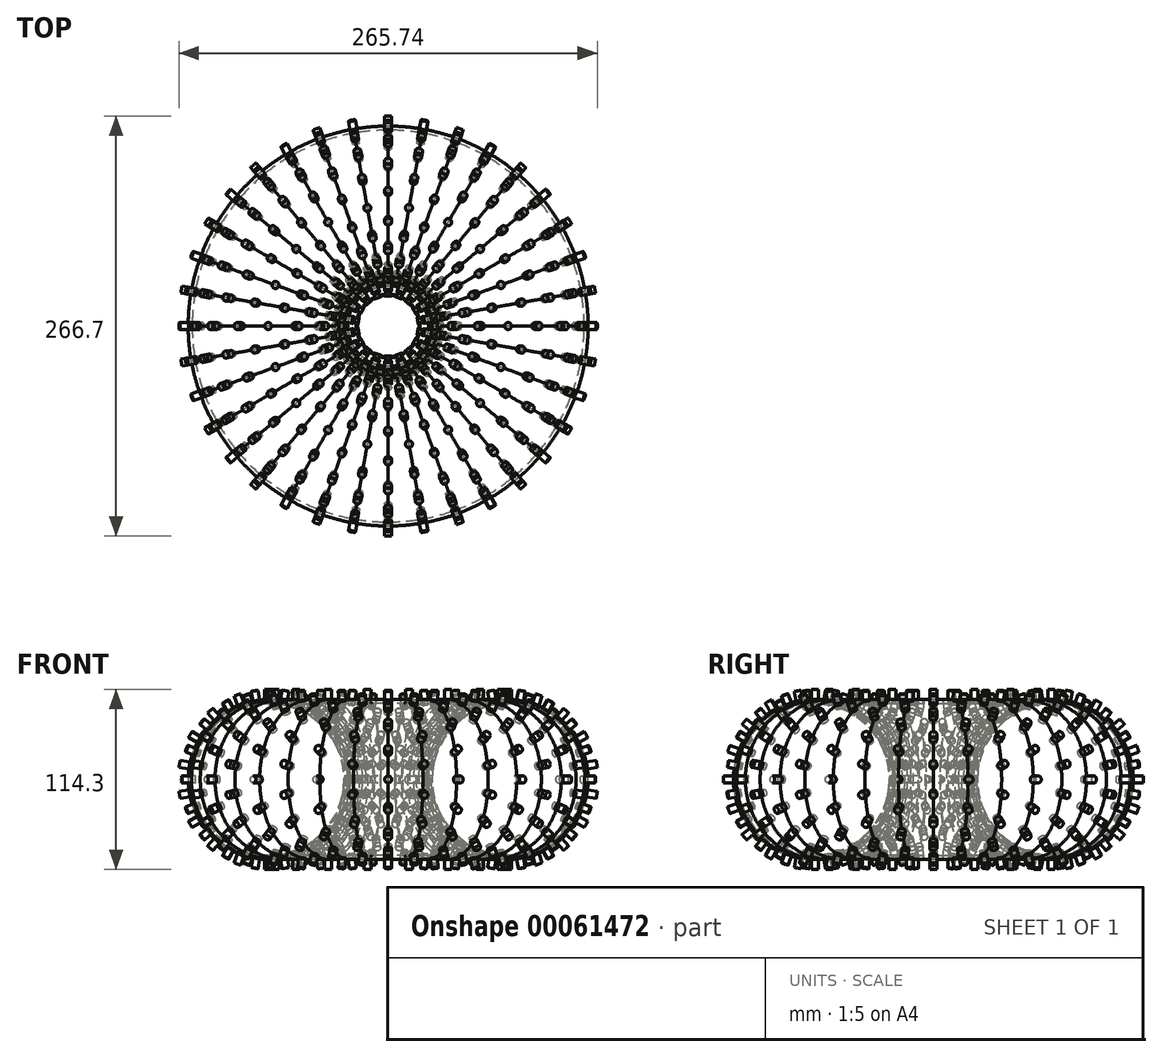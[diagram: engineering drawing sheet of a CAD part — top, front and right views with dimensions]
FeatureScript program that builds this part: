
annotation { "Feature Type Name" : "Feature", "Feature Type Description" : "" }
export const myFeature = defineFeature(function(context is Context, id is Id, definition is map)
    precondition{}
    {
        {
            var Q0;
            Q0=qCreatedBy(makeId("Top.planeOp"),FACE);
            var sketch = newSketch(context, id + "F0", { "sketchPlane" : qUnion([Q0])});
            skCircle(sketch, "E0", {"center": v(0, 0) * mm, "radius": 76.2 * mm});
            skCircle(sketch, "E1", {"center": v(0, 0) * mm, "radius": 25.4 * mm});
            skCircle(sketch, "E2", {"center": v(0, 0) * mm, "radius": 127 * mm});
            skSolve(sketch);
        }
        {
            var Q0;
            Q0=qCreatedBy(makeId("Front.planeOp"),FACE);
            cPlane(context, id + "F1", {"entities" : qUnion([Q0]), "cplaneType" : CPlaneType.OFFSET, "offset" : 25.4 * mm, "width" : 152.4 * mm, "height" : 152.4 * mm});
        }
        {
            var Q0;
            Q0=qCreatedBy(id+"F1.planeOp",FACE);
            cPlane(context, id + "F2", {"entities" : qUnion([Q0]), "cplaneType" : CPlaneType.OFFSET, "offset" : 101.6 * mm, "width" : 152.4 * mm, "height" : 152.4 * mm});
        }
        {
            var Q0;
            Q0=qCreatedBy(makeId("Right.planeOp"),FACE);
            var sketch = newSketch(context, id + "F3", { "sketchPlane" : qUnion([Q0])});
            skCircle(sketch, "E3", {"center": v(-76.2, 0) * mm, "radius": 50.8 * mm});
            skCircle(sketch, "E4", {"center": v(-76.2, 0) * mm, "radius": 48.26 * mm});
            skSolve(sketch);
        }
        {
            var Q0;
            Q0=makeQuery(id+"F3.imprint","IMPRINT",FACE,{"disambiguationData":[TD([[makeQuery(id+"F3.imprint","IMPRINT",EDGE,{"derivedFrom":sQuery(id+"F3.wireOp",EDGE,"E3")}),1.0]])]});
            var Q1;
            Q1=sQuery(id+"F0.wireOp",EDGE,"E0");
            revolve(context, id + "F4", {"entities" : qUnion([Q0]), "axis" : qUnion([Q1]), "revolveType" : RevolveType.ONE_DIRECTION, "oppositeDirection" : true, "angle" : 10 * degree});
        }
        {
            var Q0;
            Q0=makeQuery(id+"F4.opRevolve","SWEPT_BODY",BODY,{"disambiguationData":[OSD([sQuery(id+"F3.wireOp",EDGE,"E3"),sQuery(id+"F3.wireOp",EDGE,"E4")])]});
            var Q1;
            Q1=sQuery(id+"F0.wireOp",EDGE,"E0");
            circularPattern(context, id + "F5", {"entities" : qUnion([Q0]), "axis" : qUnion([Q1]), "angle" : 10 * degree, "instanceCount" : 36, "oppositeDirection" : true});
        }
        {
            var Q0;
            Q0=sQuery(id+"F0.wireOp",EDGE,"E0");
            var Q1;
            Q1=makeQuery(id+"F4.opRevolve","CAP_EDGE",EDGE,{"disambiguationData":[OSD([sQuery(id+"F3.wireOp",EDGE,"E3")])],"isStart":false});
            cPlane(context, id + "F6", {"entities" : qUnion([Q0, Q1]), "cplaneType" : CPlaneType.LINE_ANGLE, "offset" : 152.4 * mm, "angle" : 0 * degree, "width" : 152.4 * mm, "height" : 152.4 * mm});
        }
        {
            var Q0;
            Q0=qCreatedBy(id+"F6.planeOp",FACE);
            cPlane(context, id + "F7", {"entities" : qUnion([Q0]), "cplaneType" : CPlaneType.OFFSET, "offset" : 76.2 * mm, "oppositeDirection" : true, "width" : 152.4 * mm, "height" : 152.4 * mm});
        }
        {
            var Q0;
            Q0=qCreatedBy(id+"F7.planeOp",FACE);
            var sketch = newSketch(context, id + "F8", { "sketchPlane" : qUnion([Q0])});
            skLineSegment(sketch, "E5", {"start": v(29.1, 0) * mm, "end": v(-33.87, 0) * mm});
            skSolve(sketch);
        }
        {
            var Q0;
            Q0=qCreatedBy(id+"F7.planeOp",FACE);
            var Q1;
            Q1=sQuery(id+"F8.wireOp",EDGE,"E5");
            cPlane(context, id + "F9", {"entities" : qUnion([Q0, Q1]), "cplaneType" : CPlaneType.LINE_ANGLE, "offset" : 152.4 * mm, "angle" : 10 * degree, "width" : 152.4 * mm, "height" : 152.4 * mm});
        }
        {
            var Q0;
            Q0=qCreatedBy(id+"F9.planeOp",FACE);
            cPlane(context, id + "F10", {"entities" : qUnion([Q0]), "cplaneType" : CPlaneType.OFFSET, "offset" : 50.8 * mm, "width" : 152.4 * mm, "height" : 152.4 * mm});
        }
        {
            var Q0;
            Q0=qCreatedBy(id+"F2.planeOp",FACE);
            var sketch = newSketch(context, id + "F11", { "sketchPlane" : qUnion([Q0])});
            skCircle(sketch, "E6", {"center": v(0, 0) * mm, "radius": 2.22 * mm});
            skSolve(sketch);
        }
        {
            var Q0;
            Q0=makeQuery(id+"F11.imprint","IMPRINT",FACE,{"disambiguationData":[TD([[makeQuery(id+"F11.imprint","IMPRINT",EDGE,{"derivedFrom":sQuery(id+"F11.wireOp",EDGE,"E6")}),1.0]])]});
            extrude(context, id + "F12", {"entities" : qUnion([Q0]), "depth" : 6.35 * mm});
        }
        {
            var Q0;
            Q0 = qSketchRegion(id + "F11", true);
            var Q1;
            Q1=makeQuery(id+"F4.opRevolve","SWEPT_BODY",BODY,{"disambiguationData":[OSD([sQuery(id+"F3.wireOp",EDGE,"5e988a43-9d18-4499-b04f-da67374f12c3.0"),sQuery(id+"F3.wireOp",EDGE,"5e988a43-9d18-4499-b04f-da67374f12c3.1"),sQuery(id+"F3.wireOp",EDGE,"5e988a43-9d18-4499-b04f-da67374f12c3.2"),sQuery(id+"F3.wireOp",EDGE,"5e988a43-9d18-4499-b04f-da67374f12c3.3"),sQuery(id+"F3.wireOp",EDGE,"5e988a43-9d18-4499-b04f-da67374f12c3.4"),sQuery(id+"F3.wireOp",EDGE,"5e988a43-9d18-4499-b04f-da67374f12c3.5"),sQuery(id+"F3.wireOp",EDGE,"5e988a43-9d18-4499-b04f-da67374f12c3.6"),sQuery(id+"F3.wireOp",EDGE,"5e988a43-9d18-4499-b04f-da67374f12c3.7"),sQuery(id+"F3.wireOp",EDGE,"5e988a43-9d18-4499-b04f-da67374f12c3.8"),sQuery(id+"F3.wireOp",EDGE,"5e988a43-9d18-4499-b04f-da67374f12c3.9"),sQuery(id+"F3.wireOp",EDGE,"5e988a43-9d18-4499-b04f-da67374f12c3.10"),sQuery(id+"F3.wireOp",EDGE,"5e988a43-9d18-4499-b04f-da67374f12c3.11"),sQuery(id+"F3.wireOp",EDGE,"5e988a43-9d18-4499-b04f-da67374f12c3.12"),sQuery(id+"F3.wireOp",EDGE,"5e988a43-9d18-4499-b04f-da67374f12c3.13"),sQuery(id+"F3.wireOp",EDGE,"5e988a43-9d18-4499-b04f-da67374f12c3.14"),sQuery(id+"F3.wireOp",EDGE,"5e988a43-9d18-4499-b04f-da67374f12c3.15"),sQuery(id+"F3.wireOp",EDGE,"5e988a43-9d18-4499-b04f-da67374f12c3.16"),sQuery(id+"F3.wireOp",EDGE,"5e988a43-9d18-4499-b04f-da67374f12c3.17"),sQuery(id+"F3.wireOp",EDGE,"5e988a43-9d18-4499-b04f-da67374f12c3.18"),sQuery(id+"F3.wireOp",EDGE,"5e988a43-9d18-4499-b04f-da67374f12c3.19"),sQuery(id+"F3.wireOp",EDGE,"5e988a43-9d18-4499-b04f-da67374f12c3.20"),sQuery(id+"F3.wireOp",EDGE,"5e988a43-9d18-4499-b04f-da67374f12c3.21"),sQuery(id+"F3.wireOp",EDGE,"5e988a43-9d18-4499-b04f-da67374f12c3.22"),sQuery(id+"F3.wireOp",EDGE,"5e988a43-9d18-4499-b04f-da67374f12c3.23"),sQuery(id+"F3.wireOp",EDGE,"5e988a43-9d18-4499-b04f-da67374f12c3.24"),sQuery(id+"F3.wireOp",EDGE,"5e988a43-9d18-4499-b04f-da67374f12c3.25"),sQuery(id+"F3.wireOp",EDGE,"5e988a43-9d18-4499-b04f-da67374f12c3.26"),sQuery(id+"F3.wireOp",EDGE,"5e988a43-9d18-4499-b04f-da67374f12c3.27"),sQuery(id+"F3.wireOp",EDGE,"5e988a43-9d18-4499-b04f-da67374f12c3.28"),sQuery(id+"F3.wireOp",EDGE,"5e988a43-9d18-4499-b04f-da67374f12c3.29"),sQuery(id+"F3.wireOp",EDGE,"5e988a43-9d18-4499-b04f-da67374f12c3.30"),sQuery(id+"F3.wireOp",EDGE,"5e988a43-9d18-4499-b04f-da67374f12c3.31"),sQuery(id+"F3.wireOp",EDGE,"5e988a43-9d18-4499-b04f-da67374f12c3.32"),sQuery(id+"F3.wireOp",EDGE,"5e988a43-9d18-4499-b04f-da67374f12c3.33"),sQuery(id+"F3.wireOp",EDGE,"5e988a43-9d18-4499-b04f-da67374f12c3.34"),sQuery(id+"F3.wireOp",EDGE,"5e988a43-9d18-4499-b04f-da67374f12c3.35"),sQuery(id+"F3.wireOp",EDGE,"b20bae4d-07ca-4f3f-87bb-0b12c9c8b110.0"),sQuery(id+"F3.wireOp",EDGE,"b20bae4d-07ca-4f3f-87bb-0b12c9c8b110.1"),sQuery(id+"F3.wireOp",EDGE,"b20bae4d-07ca-4f3f-87bb-0b12c9c8b110.2"),sQuery(id+"F3.wireOp",EDGE,"b20bae4d-07ca-4f3f-87bb-0b12c9c8b110.3"),sQuery(id+"F3.wireOp",EDGE,"b20bae4d-07ca-4f3f-87bb-0b12c9c8b110.4"),sQuery(id+"F3.wireOp",EDGE,"b20bae4d-07ca-4f3f-87bb-0b12c9c8b110.5"),sQuery(id+"F3.wireOp",EDGE,"b20bae4d-07ca-4f3f-87bb-0b12c9c8b110.6"),sQuery(id+"F3.wireOp",EDGE,"b20bae4d-07ca-4f3f-87bb-0b12c9c8b110.7"),sQuery(id+"F3.wireOp",EDGE,"b20bae4d-07ca-4f3f-87bb-0b12c9c8b110.8"),sQuery(id+"F3.wireOp",EDGE,"b20bae4d-07ca-4f3f-87bb-0b12c9c8b110.9"),sQuery(id+"F3.wireOp",EDGE,"b20bae4d-07ca-4f3f-87bb-0b12c9c8b110.10"),sQuery(id+"F3.wireOp",EDGE,"b20bae4d-07ca-4f3f-87bb-0b12c9c8b110.11"),sQuery(id+"F3.wireOp",EDGE,"b20bae4d-07ca-4f3f-87bb-0b12c9c8b110.12"),sQuery(id+"F3.wireOp",EDGE,"b20bae4d-07ca-4f3f-87bb-0b12c9c8b110.13"),sQuery(id+"F3.wireOp",EDGE,"b20bae4d-07ca-4f3f-87bb-0b12c9c8b110.14"),sQuery(id+"F3.wireOp",EDGE,"b20bae4d-07ca-4f3f-87bb-0b12c9c8b110.15"),sQuery(id+"F3.wireOp",EDGE,"b20bae4d-07ca-4f3f-87bb-0b12c9c8b110.16"),sQuery(id+"F3.wireOp",EDGE,"b20bae4d-07ca-4f3f-87bb-0b12c9c8b110.17"),sQuery(id+"F3.wireOp",EDGE,"b20bae4d-07ca-4f3f-87bb-0b12c9c8b110.18"),sQuery(id+"F3.wireOp",EDGE,"b20bae4d-07ca-4f3f-87bb-0b12c9c8b110.19"),sQuery(id+"F3.wireOp",EDGE,"b20bae4d-07ca-4f3f-87bb-0b12c9c8b110.20"),sQuery(id+"F3.wireOp",EDGE,"b20bae4d-07ca-4f3f-87bb-0b12c9c8b110.21"),sQuery(id+"F3.wireOp",EDGE,"b20bae4d-07ca-4f3f-87bb-0b12c9c8b110.22"),sQuery(id+"F3.wireOp",EDGE,"b20bae4d-07ca-4f3f-87bb-0b12c9c8b110.23"),sQuery(id+"F3.wireOp",EDGE,"b20bae4d-07ca-4f3f-87bb-0b12c9c8b110.24"),sQuery(id+"F3.wireOp",EDGE,"b20bae4d-07ca-4f3f-87bb-0b12c9c8b110.25"),sQuery(id+"F3.wireOp",EDGE,"b20bae4d-07ca-4f3f-87bb-0b12c9c8b110.26"),sQuery(id+"F3.wireOp",EDGE,"b20bae4d-07ca-4f3f-87bb-0b12c9c8b110.27"),sQuery(id+"F3.wireOp",EDGE,"b20bae4d-07ca-4f3f-87bb-0b12c9c8b110.28"),sQuery(id+"F3.wireOp",EDGE,"b20bae4d-07ca-4f3f-87bb-0b12c9c8b110.29"),sQuery(id+"F3.wireOp",EDGE,"b20bae4d-07ca-4f3f-87bb-0b12c9c8b110.30"),sQuery(id+"F3.wireOp",EDGE,"b20bae4d-07ca-4f3f-87bb-0b12c9c8b110.31"),sQuery(id+"F3.wireOp",EDGE,"b20bae4d-07ca-4f3f-87bb-0b12c9c8b110.32"),sQuery(id+"F3.wireOp",EDGE,"b20bae4d-07ca-4f3f-87bb-0b12c9c8b110.33"),sQuery(id+"F3.wireOp",EDGE,"b20bae4d-07ca-4f3f-87bb-0b12c9c8b110.34"),sQuery(id+"F3.wireOp",EDGE,"b20bae4d-07ca-4f3f-87bb-0b12c9c8b110.35")])]});
            extrude(context, id + "F13", {"entities" : qUnion([Q0]), "oppositeDirection" : true, "endBoundEntityBody" : qUnion([Q1]), "depth" : 2.54 * mm});
        }
        {
            var Q0;
            Q0=qCreatedBy(id+"F10.planeOp",FACE);
            var sketch = newSketch(context, id + "F14", { "sketchPlane" : qUnion([Q0])});
            skCircle(sketch, "E7", {"center": v(-0.4, 13.23) * mm, "radius": 2.22 * mm});
            skSolve(sketch);
        }
        {
            var Q0;
            Q0=makeQuery(id+"F14.imprint","IMPRINT",FACE,{"disambiguationData":[TD([[makeQuery(id+"F14.imprint","IMPRINT",EDGE,{"derivedFrom":sQuery(id+"F14.wireOp",EDGE,"E7")}),1.0]])]});
            extrude(context, id + "F15", {"entities" : qUnion([Q0]), "depth" : 6.35 * mm});
        }
        {
            var Q0;
            Q0 = qSketchRegion(id + "F14", true);
            extrude(context, id + "F16", {"entities" : qUnion([Q0]), "oppositeDirection" : true, "depth" : 2.54 * mm});
        }
        {
            var Q0;
            Q0=makeQuery(id+"F12.opExtrude","SWEPT_BODY",BODY,{"disambiguationData":[OSD([sQuery(id+"F11.wireOp",EDGE,"E6")])]});
            var Q1;
            Q1=makeQuery(id+"F13.opExtrude","SWEPT_BODY",BODY,{"disambiguationData":[OSD([sQuery(id+"F11.wireOp",EDGE,"E6")])]});
            var Q2;
            Q2=sQuery(id+"F0.wireOp",EDGE,"E0");
            circularPattern(context, id + "F17", {"entities" : qUnion([Q0, Q1]), "axis" : qUnion([Q2]), "angle" : 20 * degree, "instanceCount" : 18, "oppositeDirection" : true});
        }
        {
            var Q0;
            Q0=makeQuery(id+"F15.opExtrude","SWEPT_BODY",BODY,{"disambiguationData":[OSD([sQuery(id+"F14.wireOp",EDGE,"E7")])]});
            var Q1;
            Q1=makeQuery(id+"F16.opExtrude","SWEPT_BODY",BODY,{"disambiguationData":[OSD([sQuery(id+"F14.wireOp",EDGE,"E7")])]});
            var Q2;
            Q2=sQuery(id+"F0.wireOp",EDGE,"E0");
            circularPattern(context, id + "F18", {"entities" : qUnion([Q0, Q1]), "axis" : qUnion([Q2]), "angle" : 20 * degree, "instanceCount" : 18});
        }
        {
            var Q0;
            Q0=makeQuery(id+"F18.opPattern","COPY",BODY,{"derivedFrom":makeQuery(id+"F15.opExtrude","SWEPT_BODY",BODY,{"disambiguationData":[OSD([sQuery(id+"F14.wireOp",EDGE,"E7")])]}),"instanceName":"16"});
            var Q1;
            Q1=makeQuery(id+"F18.opPattern","COPY",BODY,{"derivedFrom":makeQuery(id+"F16.opExtrude","SWEPT_BODY",BODY,{"disambiguationData":[OSD([sQuery(id+"F14.wireOp",EDGE,"E7")])]}),"instanceName":"16"});
            var Q2;
            Q2=makeQuery(id+"F5.opPattern","COPY",EDGE,{"derivedFrom":makeQuery(id+"F4.opRevolve","CAP_EDGE",EDGE,{"disambiguationData":[OSD([sQuery(id+"F3.wireOp",EDGE,"E3")])],"isStart":true}),"instanceName":"5"});
            circularPattern(context, id + "F19", {"entities" : qUnion([Q0, Q1]), "axis" : qUnion([Q2]), "angle" : 20 * degree, "instanceCount" : 18});
        }
        {
            var Q0;
            Q0=makeQuery(id+"F17.opPattern","COPY",BODY,{"derivedFrom":makeQuery(id+"F12.opExtrude","SWEPT_BODY",BODY,{"disambiguationData":[OSD([sQuery(id+"F11.wireOp",EDGE,"E6")])]}),"instanceName":"3"});
            var Q1;
            Q1=makeQuery(id+"F17.opPattern","COPY",BODY,{"derivedFrom":makeQuery(id+"F13.opExtrude","SWEPT_BODY",BODY,{"disambiguationData":[OSD([sQuery(id+"F11.wireOp",EDGE,"E6")])]}),"instanceName":"3"});
            var Q2;
            Q2=makeQuery(id+"F5.opPattern","COPY",EDGE,{"derivedFrom":makeQuery(id+"F4.opRevolve","CAP_EDGE",EDGE,{"disambiguationData":[OSD([sQuery(id+"F3.wireOp",EDGE,"E3")])],"isStart":false}),"instanceName":"5"});
            circularPattern(context, id + "F20", {"entities" : qUnion([Q0, Q1]), "axis" : qUnion([Q2]), "angle" : 20 * degree, "instanceCount" : 18});
        }
        {
            var Q0;
            Q0=makeQuery(id+"F18.opPattern","COPY",BODY,{"derivedFrom":makeQuery(id+"F16.opExtrude","SWEPT_BODY",BODY,{"disambiguationData":[OSD([sQuery(id+"F14.wireOp",EDGE,"E7")])]}),"instanceName":"15"});
            var Q1;
            Q1=makeQuery(id+"F18.opPattern","COPY",BODY,{"derivedFrom":makeQuery(id+"F15.opExtrude","SWEPT_BODY",BODY,{"disambiguationData":[OSD([sQuery(id+"F14.wireOp",EDGE,"E7")])]}),"instanceName":"15"});
            var Q2;
            Q2=makeQuery(id+"F5.opPattern","COPY",EDGE,{"derivedFrom":makeQuery(id+"F4.opRevolve","CAP_EDGE",EDGE,{"disambiguationData":[OSD([sQuery(id+"F3.wireOp",EDGE,"E3")])],"isStart":false}),"instanceName":"6"});
            circularPattern(context, id + "F21", {"entities" : qUnion([Q0, Q1]), "axis" : qUnion([Q2]), "angle" : 20 * degree, "instanceCount" : 18});
        }
        {
            var Q0;
            Q0=makeQuery(id+"F17.opPattern","COPY",BODY,{"derivedFrom":makeQuery(id+"F12.opExtrude","SWEPT_BODY",BODY,{"disambiguationData":[OSD([sQuery(id+"F11.wireOp",EDGE,"E6")])]}),"instanceName":"4"});
            var Q1;
            Q1=makeQuery(id+"F17.opPattern","COPY",BODY,{"derivedFrom":makeQuery(id+"F13.opExtrude","SWEPT_BODY",BODY,{"disambiguationData":[OSD([sQuery(id+"F11.wireOp",EDGE,"E6")])]}),"instanceName":"4"});
            var Q2;
            Q2=makeQuery(id+"F5.opPattern","COPY",EDGE,{"derivedFrom":makeQuery(id+"F4.opRevolve","CAP_EDGE",EDGE,{"disambiguationData":[OSD([sQuery(id+"F3.wireOp",EDGE,"E3")])],"isStart":false}),"instanceName":"7"});
            circularPattern(context, id + "F22", {"entities" : qUnion([Q0, Q1]), "axis" : qUnion([Q2]), "angle" : 20 * degree, "instanceCount" : 18});
        }
        {
            var Q0;
            Q0=makeQuery(id+"F18.opPattern","COPY",BODY,{"derivedFrom":makeQuery(id+"F15.opExtrude","SWEPT_BODY",BODY,{"disambiguationData":[OSD([sQuery(id+"F14.wireOp",EDGE,"E7")])]}),"instanceName":"14"});
            var Q1;
            Q1=makeQuery(id+"F18.opPattern","COPY",BODY,{"derivedFrom":makeQuery(id+"F16.opExtrude","SWEPT_BODY",BODY,{"disambiguationData":[OSD([sQuery(id+"F14.wireOp",EDGE,"E7")])]}),"instanceName":"14"});
            var Q2;
            Q2=makeQuery(id+"F5.opPattern","COPY",EDGE,{"derivedFrom":makeQuery(id+"F4.opRevolve","CAP_EDGE",EDGE,{"disambiguationData":[OSD([sQuery(id+"F3.wireOp",EDGE,"E3")])],"isStart":true}),"instanceName":"9"});
            circularPattern(context, id + "F23", {"entities" : qUnion([Q0, Q1]), "axis" : qUnion([Q2]), "angle" : 20 * degree, "instanceCount" : 18});
        }
        {
            var Q0;
            Q0=makeQuery(id+"F17.opPattern","COPY",BODY,{"derivedFrom":makeQuery(id+"F12.opExtrude","SWEPT_BODY",BODY,{"disambiguationData":[OSD([sQuery(id+"F11.wireOp",EDGE,"E6")])]}),"instanceName":"5"});
            var Q1;
            Q1=makeQuery(id+"F17.opPattern","COPY",BODY,{"derivedFrom":makeQuery(id+"F13.opExtrude","SWEPT_BODY",BODY,{"disambiguationData":[OSD([sQuery(id+"F11.wireOp",EDGE,"E6")])]}),"instanceName":"5"});
            var Q2;
            Q2=makeQuery(id+"F5.opPattern","COPY",EDGE,{"derivedFrom":makeQuery(id+"F4.opRevolve","CAP_EDGE",EDGE,{"disambiguationData":[OSD([sQuery(id+"F3.wireOp",EDGE,"E3")])],"isStart":true}),"instanceName":"10"});
            circularPattern(context, id + "F24", {"entities" : qUnion([Q0, Q1]), "axis" : qUnion([Q2]), "angle" : 20 * degree, "instanceCount" : 18});
        }
        {
            var Q0;
            Q0=makeQuery(id+"F18.opPattern","COPY",BODY,{"derivedFrom":makeQuery(id+"F15.opExtrude","SWEPT_BODY",BODY,{"disambiguationData":[OSD([sQuery(id+"F14.wireOp",EDGE,"E7")])]}),"instanceName":"13"});
            var Q1;
            Q1=makeQuery(id+"F18.opPattern","COPY",BODY,{"derivedFrom":makeQuery(id+"F16.opExtrude","SWEPT_BODY",BODY,{"disambiguationData":[OSD([sQuery(id+"F14.wireOp",EDGE,"E7")])]}),"instanceName":"13"});
            var Q2;
            Q2=makeQuery(id+"F5.opPattern","COPY",EDGE,{"derivedFrom":makeQuery(id+"F4.opRevolve","CAP_EDGE",EDGE,{"disambiguationData":[OSD([sQuery(id+"F3.wireOp",EDGE,"E3")])],"isStart":true}),"instanceName":"11"});
            circularPattern(context, id + "F25", {"entities" : qUnion([Q0, Q1]), "axis" : qUnion([Q2]), "angle" : 20 * degree, "instanceCount" : 18});
        }
        {
            var Q0;
            Q0=makeQuery(id+"F17.opPattern","COPY",BODY,{"derivedFrom":makeQuery(id+"F12.opExtrude","SWEPT_BODY",BODY,{"disambiguationData":[OSD([sQuery(id+"F11.wireOp",EDGE,"E6")])]}),"instanceName":"6"});
            var Q1;
            Q1=makeQuery(id+"F17.opPattern","COPY",BODY,{"derivedFrom":makeQuery(id+"F13.opExtrude","SWEPT_BODY",BODY,{"disambiguationData":[OSD([sQuery(id+"F11.wireOp",EDGE,"E6")])]}),"instanceName":"6"});
            var Q2;
            Q2=makeQuery(id+"F5.opPattern","COPY",EDGE,{"derivedFrom":makeQuery(id+"F4.opRevolve","CAP_EDGE",EDGE,{"disambiguationData":[OSD([sQuery(id+"F3.wireOp",EDGE,"E3")])],"isStart":true}),"instanceName":"12"});
            circularPattern(context, id + "F26", {"entities" : qUnion([Q0, Q1]), "axis" : qUnion([Q2]), "angle" : 20 * degree, "instanceCount" : 18});
        }
        {
            var Q0;
            Q0=makeQuery(id+"F18.opPattern","COPY",BODY,{"derivedFrom":makeQuery(id+"F15.opExtrude","SWEPT_BODY",BODY,{"disambiguationData":[OSD([sQuery(id+"F14.wireOp",EDGE,"E7")])]}),"instanceName":"12"});
            var Q1;
            Q1=makeQuery(id+"F18.opPattern","COPY",BODY,{"derivedFrom":makeQuery(id+"F16.opExtrude","SWEPT_BODY",BODY,{"disambiguationData":[OSD([sQuery(id+"F14.wireOp",EDGE,"E7")])]}),"instanceName":"12"});
            var Q2;
            Q2=makeQuery(id+"F5.opPattern","COPY",EDGE,{"derivedFrom":makeQuery(id+"F4.opRevolve","CAP_EDGE",EDGE,{"disambiguationData":[OSD([sQuery(id+"F3.wireOp",EDGE,"E3")])],"isStart":true}),"instanceName":"13"});
            circularPattern(context, id + "F27", {"entities" : qUnion([Q0, Q1]), "axis" : qUnion([Q2]), "angle" : 20 * degree, "instanceCount" : 18});
        }
        {
            var Q0;
            Q0=makeQuery(id+"F17.opPattern","COPY",BODY,{"derivedFrom":makeQuery(id+"F13.opExtrude","SWEPT_BODY",BODY,{"disambiguationData":[OSD([sQuery(id+"F11.wireOp",EDGE,"E6")])]}),"instanceName":"7"});
            var Q1;
            Q1=makeQuery(id+"F17.opPattern","COPY",BODY,{"derivedFrom":makeQuery(id+"F12.opExtrude","SWEPT_BODY",BODY,{"disambiguationData":[OSD([sQuery(id+"F11.wireOp",EDGE,"E6")])]}),"instanceName":"7"});
            var Q2;
            Q2=makeQuery(id+"F5.opPattern","COPY",EDGE,{"derivedFrom":makeQuery(id+"F4.opRevolve","CAP_EDGE",EDGE,{"disambiguationData":[OSD([sQuery(id+"F3.wireOp",EDGE,"E3")])],"isStart":false}),"instanceName":"13"});
            circularPattern(context, id + "F28", {"entities" : qUnion([Q0, Q1]), "axis" : qUnion([Q2]), "angle" : 20 * degree, "instanceCount" : 18});
        }
        {
            var Q0;
            Q0=makeQuery(id+"F18.opPattern","COPY",BODY,{"derivedFrom":makeQuery(id+"F16.opExtrude","SWEPT_BODY",BODY,{"disambiguationData":[OSD([sQuery(id+"F14.wireOp",EDGE,"E7")])]}),"instanceName":"11"});
            var Q1;
            Q1=makeQuery(id+"F18.opPattern","COPY",BODY,{"derivedFrom":makeQuery(id+"F15.opExtrude","SWEPT_BODY",BODY,{"disambiguationData":[OSD([sQuery(id+"F14.wireOp",EDGE,"E7")])]}),"instanceName":"11"});
            var Q2;
            Q2=makeQuery(id+"F5.opPattern","COPY",EDGE,{"derivedFrom":makeQuery(id+"F4.opRevolve","CAP_EDGE",EDGE,{"disambiguationData":[OSD([sQuery(id+"F3.wireOp",EDGE,"E3")])],"isStart":false}),"instanceName":"14"});
            circularPattern(context, id + "F29", {"entities" : qUnion([Q0, Q1]), "axis" : qUnion([Q2]), "angle" : 20 * degree, "instanceCount" : 18});
        }
        {
            var Q0;
            Q0=makeQuery(id+"F17.opPattern","COPY",BODY,{"derivedFrom":makeQuery(id+"F13.opExtrude","SWEPT_BODY",BODY,{"disambiguationData":[OSD([sQuery(id+"F11.wireOp",EDGE,"E6")])]}),"instanceName":"8"});
            var Q1;
            Q1=makeQuery(id+"F17.opPattern","COPY",BODY,{"derivedFrom":makeQuery(id+"F12.opExtrude","SWEPT_BODY",BODY,{"disambiguationData":[OSD([sQuery(id+"F11.wireOp",EDGE,"E6")])]}),"instanceName":"8"});
            var Q2;
            Q2=makeQuery(id+"F5.opPattern","COPY",EDGE,{"derivedFrom":makeQuery(id+"F4.opRevolve","CAP_EDGE",EDGE,{"disambiguationData":[OSD([sQuery(id+"F3.wireOp",EDGE,"E3")])],"isStart":false}),"instanceName":"15"});
            circularPattern(context, id + "F30", {"entities" : qUnion([Q0, Q1]), "axis" : qUnion([Q2]), "angle" : 20 * degree, "instanceCount" : 18});
        }
        {
            var Q0;
            Q0=makeQuery(id+"F18.opPattern","COPY",BODY,{"derivedFrom":makeQuery(id+"F16.opExtrude","SWEPT_BODY",BODY,{"disambiguationData":[OSD([sQuery(id+"F14.wireOp",EDGE,"E7")])]}),"instanceName":"10"});
            var Q1;
            Q1=makeQuery(id+"F18.opPattern","COPY",BODY,{"derivedFrom":makeQuery(id+"F15.opExtrude","SWEPT_BODY",BODY,{"disambiguationData":[OSD([sQuery(id+"F14.wireOp",EDGE,"E7")])]}),"instanceName":"10"});
            var Q2;
            Q2=makeQuery(id+"F5.opPattern","COPY",EDGE,{"derivedFrom":makeQuery(id+"F4.opRevolve","CAP_EDGE",EDGE,{"disambiguationData":[OSD([sQuery(id+"F3.wireOp",EDGE,"E3")])],"isStart":false}),"instanceName":"16"});
            circularPattern(context, id + "F31", {"entities" : qUnion([Q0, Q1]), "axis" : qUnion([Q2]), "angle" : 20 * degree, "instanceCount" : 18});
        }
        {
            var Q0;
            Q0=makeQuery(id+"F17.opPattern","COPY",BODY,{"derivedFrom":makeQuery(id+"F13.opExtrude","SWEPT_BODY",BODY,{"disambiguationData":[OSD([sQuery(id+"F11.wireOp",EDGE,"E6")])]}),"instanceName":"9"});
            var Q1;
            Q1=makeQuery(id+"F17.opPattern","COPY",BODY,{"derivedFrom":makeQuery(id+"F12.opExtrude","SWEPT_BODY",BODY,{"disambiguationData":[OSD([sQuery(id+"F11.wireOp",EDGE,"E6")])]}),"instanceName":"9"});
            var Q2;
            Q2=makeQuery(id+"F5.opPattern","COPY",EDGE,{"derivedFrom":makeQuery(id+"F4.opRevolve","CAP_EDGE",EDGE,{"disambiguationData":[OSD([sQuery(id+"F3.wireOp",EDGE,"E3")])],"isStart":true}),"instanceName":"18"});
            circularPattern(context, id + "F32", {"entities" : qUnion([Q0, Q1]), "axis" : qUnion([Q2]), "angle" : 20 * degree, "instanceCount" : 18});
        }
        {
            var Q0;
            Q0=makeQuery(id+"F18.opPattern","COPY",BODY,{"derivedFrom":makeQuery(id+"F16.opExtrude","SWEPT_BODY",BODY,{"disambiguationData":[OSD([sQuery(id+"F14.wireOp",EDGE,"E7")])]}),"instanceName":"9"});
            var Q1;
            Q1=makeQuery(id+"F18.opPattern","COPY",BODY,{"derivedFrom":makeQuery(id+"F15.opExtrude","SWEPT_BODY",BODY,{"disambiguationData":[OSD([sQuery(id+"F14.wireOp",EDGE,"E7")])]}),"instanceName":"9"});
            var Q2;
            Q2=makeQuery(id+"F5.opPattern","COPY",EDGE,{"derivedFrom":makeQuery(id+"F4.opRevolve","CAP_EDGE",EDGE,{"disambiguationData":[OSD([sQuery(id+"F3.wireOp",EDGE,"E3")])],"isStart":true}),"instanceName":"19"});
            circularPattern(context, id + "F33", {"entities" : qUnion([Q0, Q1]), "axis" : qUnion([Q2]), "angle" : 20 * degree, "instanceCount" : 18});
        }
        {
            var Q0;
            Q0=makeQuery(id+"F17.opPattern","COPY",BODY,{"derivedFrom":makeQuery(id+"F12.opExtrude","SWEPT_BODY",BODY,{"disambiguationData":[OSD([sQuery(id+"F11.wireOp",EDGE,"E6")])]}),"instanceName":"10"});
            var Q1;
            Q1=makeQuery(id+"F17.opPattern","COPY",BODY,{"derivedFrom":makeQuery(id+"F13.opExtrude","SWEPT_BODY",BODY,{"disambiguationData":[OSD([sQuery(id+"F11.wireOp",EDGE,"E6")])]}),"instanceName":"10"});
            var Q2;
            Q2=makeQuery(id+"F5.opPattern","COPY",EDGE,{"derivedFrom":makeQuery(id+"F4.opRevolve","CAP_EDGE",EDGE,{"disambiguationData":[OSD([sQuery(id+"F3.wireOp",EDGE,"E3")])],"isStart":true}),"instanceName":"20"});
            circularPattern(context, id + "F34", {"entities" : qUnion([Q0, Q1]), "axis" : qUnion([Q2]), "angle" : 20 * degree, "instanceCount" : 18});
        }
        {
            var Q0;
            Q0=makeQuery(id+"F18.opPattern","COPY",BODY,{"derivedFrom":makeQuery(id+"F15.opExtrude","SWEPT_BODY",BODY,{"disambiguationData":[OSD([sQuery(id+"F14.wireOp",EDGE,"E7")])]}),"instanceName":"8"});
            var Q1;
            Q1=makeQuery(id+"F18.opPattern","COPY",BODY,{"derivedFrom":makeQuery(id+"F16.opExtrude","SWEPT_BODY",BODY,{"disambiguationData":[OSD([sQuery(id+"F14.wireOp",EDGE,"E7")])]}),"instanceName":"8"});
            var Q2;
            Q2=makeQuery(id+"F5.opPattern","COPY",EDGE,{"derivedFrom":makeQuery(id+"F4.opRevolve","CAP_EDGE",EDGE,{"disambiguationData":[OSD([sQuery(id+"F3.wireOp",EDGE,"E3")])],"isStart":true}),"instanceName":"21"});
            circularPattern(context, id + "F35", {"entities" : qUnion([Q0, Q1]), "axis" : qUnion([Q2]), "angle" : 20 * degree, "instanceCount" : 18});
        }
        {
            var Q0;
            Q0=makeQuery(id+"F17.opPattern","COPY",BODY,{"derivedFrom":makeQuery(id+"F13.opExtrude","SWEPT_BODY",BODY,{"disambiguationData":[OSD([sQuery(id+"F11.wireOp",EDGE,"E6")])]}),"instanceName":"11"});
            var Q1;
            Q1=makeQuery(id+"F17.opPattern","COPY",BODY,{"derivedFrom":makeQuery(id+"F12.opExtrude","SWEPT_BODY",BODY,{"disambiguationData":[OSD([sQuery(id+"F11.wireOp",EDGE,"E6")])]}),"instanceName":"11"});
            var Q2;
            Q2=makeQuery(id+"F5.opPattern","COPY",EDGE,{"derivedFrom":makeQuery(id+"F4.opRevolve","CAP_EDGE",EDGE,{"disambiguationData":[OSD([sQuery(id+"F3.wireOp",EDGE,"E3")])],"isStart":true}),"instanceName":"22"});
            circularPattern(context, id + "F36", {"entities" : qUnion([Q0, Q1]), "axis" : qUnion([Q2]), "angle" : 20 * degree, "instanceCount" : 18});
        }
        {
            var Q0;
            Q0=makeQuery(id+"F18.opPattern","COPY",BODY,{"derivedFrom":makeQuery(id+"F16.opExtrude","SWEPT_BODY",BODY,{"disambiguationData":[OSD([sQuery(id+"F14.wireOp",EDGE,"E7")])]}),"instanceName":"7"});
            var Q1;
            Q1=makeQuery(id+"F18.opPattern","COPY",BODY,{"derivedFrom":makeQuery(id+"F15.opExtrude","SWEPT_BODY",BODY,{"disambiguationData":[OSD([sQuery(id+"F14.wireOp",EDGE,"E7")])]}),"instanceName":"7"});
            var Q2;
            Q2=makeQuery(id+"F5.opPattern","COPY",EDGE,{"derivedFrom":makeQuery(id+"F4.opRevolve","CAP_EDGE",EDGE,{"disambiguationData":[OSD([sQuery(id+"F3.wireOp",EDGE,"E3")])],"isStart":false}),"instanceName":"22"});
            circularPattern(context, id + "F37", {"entities" : qUnion([Q0, Q1]), "axis" : qUnion([Q2]), "angle" : 20 * degree, "instanceCount" : 18});
        }
        {
            var Q0;
            Q0=makeQuery(id+"F17.opPattern","COPY",BODY,{"derivedFrom":makeQuery(id+"F12.opExtrude","SWEPT_BODY",BODY,{"disambiguationData":[OSD([sQuery(id+"F11.wireOp",EDGE,"E6")])]}),"instanceName":"12"});
            var Q1;
            Q1=makeQuery(id+"F17.opPattern","COPY",BODY,{"derivedFrom":makeQuery(id+"F13.opExtrude","SWEPT_BODY",BODY,{"disambiguationData":[OSD([sQuery(id+"F11.wireOp",EDGE,"E6")])]}),"instanceName":"12"});
            var Q2;
            Q2=makeQuery(id+"F5.opPattern","COPY",EDGE,{"derivedFrom":makeQuery(id+"F4.opRevolve","CAP_EDGE",EDGE,{"disambiguationData":[OSD([sQuery(id+"F3.wireOp",EDGE,"E3")])],"isStart":false}),"instanceName":"23"});
            circularPattern(context, id + "F38", {"entities" : qUnion([Q0, Q1]), "axis" : qUnion([Q2]), "angle" : 20 * degree, "instanceCount" : 18});
        }
        {
            var Q0;
            Q0=makeQuery(id+"F18.opPattern","COPY",BODY,{"derivedFrom":makeQuery(id+"F15.opExtrude","SWEPT_BODY",BODY,{"disambiguationData":[OSD([sQuery(id+"F14.wireOp",EDGE,"E7")])]}),"instanceName":"6"});
            var Q1;
            Q1=makeQuery(id+"F18.opPattern","COPY",BODY,{"derivedFrom":makeQuery(id+"F16.opExtrude","SWEPT_BODY",BODY,{"disambiguationData":[OSD([sQuery(id+"F14.wireOp",EDGE,"E7")])]}),"instanceName":"6"});
            var Q2;
            Q2=makeQuery(id+"F5.opPattern","COPY",EDGE,{"derivedFrom":makeQuery(id+"F4.opRevolve","CAP_EDGE",EDGE,{"disambiguationData":[OSD([sQuery(id+"F3.wireOp",EDGE,"E3")])],"isStart":false}),"instanceName":"24"});
            circularPattern(context, id + "F39", {"entities" : qUnion([Q0, Q1]), "axis" : qUnion([Q2]), "angle" : 20 * degree, "instanceCount" : 18});
        }
        {
            var Q0;
            Q0=makeQuery(id+"F17.opPattern","COPY",BODY,{"derivedFrom":makeQuery(id+"F12.opExtrude","SWEPT_BODY",BODY,{"disambiguationData":[OSD([sQuery(id+"F11.wireOp",EDGE,"E6")])]}),"instanceName":"13"});
            var Q1;
            Q1=makeQuery(id+"F17.opPattern","COPY",BODY,{"derivedFrom":makeQuery(id+"F13.opExtrude","SWEPT_BODY",BODY,{"disambiguationData":[OSD([sQuery(id+"F11.wireOp",EDGE,"E6")])]}),"instanceName":"13"});
            var Q2;
            Q2=makeQuery(id+"F5.opPattern","COPY",EDGE,{"derivedFrom":makeQuery(id+"F4.opRevolve","CAP_EDGE",EDGE,{"disambiguationData":[OSD([sQuery(id+"F3.wireOp",EDGE,"E3")])],"isStart":false}),"instanceName":"25"});
            circularPattern(context, id + "F40", {"entities" : qUnion([Q0, Q1]), "axis" : qUnion([Q2]), "angle" : 20 * degree, "instanceCount" : 18});
        }
        {
            var Q0;
            Q0=makeQuery(id+"F18.opPattern","COPY",BODY,{"derivedFrom":makeQuery(id+"F15.opExtrude","SWEPT_BODY",BODY,{"disambiguationData":[OSD([sQuery(id+"F14.wireOp",EDGE,"E7")])]}),"instanceName":"5"});
            var Q1;
            Q1=makeQuery(id+"F18.opPattern","COPY",BODY,{"derivedFrom":makeQuery(id+"F16.opExtrude","SWEPT_BODY",BODY,{"disambiguationData":[OSD([sQuery(id+"F14.wireOp",EDGE,"E7")])]}),"instanceName":"5"});
            var Q2;
            Q2=makeQuery(id+"F5.opPattern","COPY",EDGE,{"derivedFrom":makeQuery(id+"F4.opRevolve","CAP_EDGE",EDGE,{"disambiguationData":[OSD([sQuery(id+"F3.wireOp",EDGE,"E3")])],"isStart":false}),"instanceName":"26"});
            circularPattern(context, id + "F41", {"entities" : qUnion([Q0, Q1]), "axis" : qUnion([Q2]), "angle" : 20 * degree, "instanceCount" : 18});
        }
        {
            var Q0;
            Q0=makeQuery(id+"F17.opPattern","COPY",BODY,{"derivedFrom":makeQuery(id+"F12.opExtrude","SWEPT_BODY",BODY,{"disambiguationData":[OSD([sQuery(id+"F11.wireOp",EDGE,"E6")])]}),"instanceName":"14"});
            var Q1;
            Q1=makeQuery(id+"F17.opPattern","COPY",BODY,{"derivedFrom":makeQuery(id+"F13.opExtrude","SWEPT_BODY",BODY,{"disambiguationData":[OSD([sQuery(id+"F11.wireOp",EDGE,"E6")])]}),"instanceName":"14"});
            var Q2;
            Q2=makeQuery(id+"F5.opPattern","COPY",EDGE,{"derivedFrom":makeQuery(id+"F4.opRevolve","CAP_EDGE",EDGE,{"disambiguationData":[OSD([sQuery(id+"F3.wireOp",EDGE,"E3")])],"isStart":true}),"instanceName":"28"});
            circularPattern(context, id + "F42", {"entities" : qUnion([Q0, Q1]), "axis" : qUnion([Q2]), "angle" : 20 * degree, "instanceCount" : 18});
        }
        {
            var Q0;
            Q0=makeQuery(id+"F18.opPattern","COPY",BODY,{"derivedFrom":makeQuery(id+"F15.opExtrude","SWEPT_BODY",BODY,{"disambiguationData":[OSD([sQuery(id+"F14.wireOp",EDGE,"E7")])]}),"instanceName":"4"});
            var Q1;
            Q1=makeQuery(id+"F18.opPattern","COPY",BODY,{"derivedFrom":makeQuery(id+"F16.opExtrude","SWEPT_BODY",BODY,{"disambiguationData":[OSD([sQuery(id+"F14.wireOp",EDGE,"E7")])]}),"instanceName":"4"});
            var Q2;
            Q2=makeQuery(id+"F5.opPattern","COPY",EDGE,{"derivedFrom":makeQuery(id+"F4.opRevolve","CAP_EDGE",EDGE,{"disambiguationData":[OSD([sQuery(id+"F3.wireOp",EDGE,"E3")])],"isStart":true}),"instanceName":"29"});
            circularPattern(context, id + "F43", {"entities" : qUnion([Q0, Q1]), "axis" : qUnion([Q2]), "angle" : 20 * degree, "instanceCount" : 18});
        }
        {
            var Q0;
            Q0=makeQuery(id+"F17.opPattern","COPY",BODY,{"derivedFrom":makeQuery(id+"F12.opExtrude","SWEPT_BODY",BODY,{"disambiguationData":[OSD([sQuery(id+"F11.wireOp",EDGE,"E6")])]}),"instanceName":"15"});
            var Q1;
            Q1=makeQuery(id+"F17.opPattern","COPY",BODY,{"derivedFrom":makeQuery(id+"F13.opExtrude","SWEPT_BODY",BODY,{"disambiguationData":[OSD([sQuery(id+"F11.wireOp",EDGE,"E6")])]}),"instanceName":"15"});
            var Q2;
            Q2=makeQuery(id+"F5.opPattern","COPY",EDGE,{"derivedFrom":makeQuery(id+"F4.opRevolve","CAP_EDGE",EDGE,{"disambiguationData":[OSD([sQuery(id+"F3.wireOp",EDGE,"E3")])],"isStart":true}),"instanceName":"30"});
            circularPattern(context, id + "F44", {"entities" : qUnion([Q0, Q1]), "axis" : qUnion([Q2]), "angle" : 20 * degree, "instanceCount" : 18});
        }
        {
            var Q0;
            Q0=makeQuery(id+"F18.opPattern","COPY",BODY,{"derivedFrom":makeQuery(id+"F15.opExtrude","SWEPT_BODY",BODY,{"disambiguationData":[OSD([sQuery(id+"F14.wireOp",EDGE,"E7")])]}),"instanceName":"3"});
            var Q1;
            Q1=makeQuery(id+"F18.opPattern","COPY",BODY,{"derivedFrom":makeQuery(id+"F16.opExtrude","SWEPT_BODY",BODY,{"disambiguationData":[OSD([sQuery(id+"F14.wireOp",EDGE,"E7")])]}),"instanceName":"3"});
            var Q2;
            Q2=makeQuery(id+"F5.opPattern","COPY",EDGE,{"derivedFrom":makeQuery(id+"F4.opRevolve","CAP_EDGE",EDGE,{"disambiguationData":[OSD([sQuery(id+"F3.wireOp",EDGE,"E3")])],"isStart":true}),"instanceName":"31"});
            circularPattern(context, id + "F45", {"entities" : qUnion([Q0, Q1]), "axis" : qUnion([Q2]), "angle" : 20 * degree, "instanceCount" : 18});
        }
        {
            var Q0;
            Q0=makeQuery(id+"F17.opPattern","COPY",BODY,{"derivedFrom":makeQuery(id+"F12.opExtrude","SWEPT_BODY",BODY,{"disambiguationData":[OSD([sQuery(id+"F11.wireOp",EDGE,"E6")])]}),"instanceName":"16"});
            var Q1;
            Q1=makeQuery(id+"F17.opPattern","COPY",BODY,{"derivedFrom":makeQuery(id+"F13.opExtrude","SWEPT_BODY",BODY,{"disambiguationData":[OSD([sQuery(id+"F11.wireOp",EDGE,"E6")])]}),"instanceName":"16"});
            var Q2;
            Q2=makeQuery(id+"F5.opPattern","COPY",EDGE,{"derivedFrom":makeQuery(id+"F4.opRevolve","CAP_EDGE",EDGE,{"disambiguationData":[OSD([sQuery(id+"F3.wireOp",EDGE,"E3")])],"isStart":false}),"instanceName":"31"});
            circularPattern(context, id + "F46", {"entities" : qUnion([Q0, Q1]), "axis" : qUnion([Q2]), "angle" : 20 * degree, "instanceCount" : 18});
        }
        {
            var Q0;
            Q0=makeQuery(id+"F18.opPattern","COPY",BODY,{"derivedFrom":makeQuery(id+"F15.opExtrude","SWEPT_BODY",BODY,{"disambiguationData":[OSD([sQuery(id+"F14.wireOp",EDGE,"E7")])]}),"instanceName":"2"});
            var Q1;
            Q1=makeQuery(id+"F18.opPattern","COPY",BODY,{"derivedFrom":makeQuery(id+"F16.opExtrude","SWEPT_BODY",BODY,{"disambiguationData":[OSD([sQuery(id+"F14.wireOp",EDGE,"E7")])]}),"instanceName":"2"});
            var Q2;
            Q2=makeQuery(id+"F5.opPattern","COPY",EDGE,{"derivedFrom":makeQuery(id+"F4.opRevolve","CAP_EDGE",EDGE,{"disambiguationData":[OSD([sQuery(id+"F3.wireOp",EDGE,"E3")])],"isStart":false}),"instanceName":"32"});
            circularPattern(context, id + "F47", {"entities" : qUnion([Q0, Q1]), "axis" : qUnion([Q2]), "angle" : 20 * degree, "instanceCount" : 18});
        }
        {
            var Q0;
            Q0=makeQuery(id+"F17.opPattern","COPY",BODY,{"derivedFrom":makeQuery(id+"F12.opExtrude","SWEPT_BODY",BODY,{"disambiguationData":[OSD([sQuery(id+"F11.wireOp",EDGE,"E6")])]}),"instanceName":"17"});
            var Q1;
            Q1=makeQuery(id+"F17.opPattern","COPY",BODY,{"derivedFrom":makeQuery(id+"F13.opExtrude","SWEPT_BODY",BODY,{"disambiguationData":[OSD([sQuery(id+"F11.wireOp",EDGE,"E6")])]}),"instanceName":"17"});
            var Q2;
            Q2=makeQuery(id+"F5.opPattern","COPY",EDGE,{"derivedFrom":makeQuery(id+"F4.opRevolve","CAP_EDGE",EDGE,{"disambiguationData":[OSD([sQuery(id+"F3.wireOp",EDGE,"E3")])],"isStart":false}),"instanceName":"33"});
            circularPattern(context, id + "F48", {"entities" : qUnion([Q0, Q1]), "axis" : qUnion([Q2]), "angle" : 20 * degree, "instanceCount" : 18});
        }
        {
            var Q0;
            Q0=makeQuery(id+"F18.opPattern","COPY",BODY,{"derivedFrom":makeQuery(id+"F15.opExtrude","SWEPT_BODY",BODY,{"disambiguationData":[OSD([sQuery(id+"F14.wireOp",EDGE,"E7")])]}),"instanceName":"1"});
            var Q1;
            Q1=makeQuery(id+"F18.opPattern","COPY",BODY,{"derivedFrom":makeQuery(id+"F16.opExtrude","SWEPT_BODY",BODY,{"disambiguationData":[OSD([sQuery(id+"F14.wireOp",EDGE,"E7")])]}),"instanceName":"1"});
            var Q2;
            Q2=makeQuery(id+"F5.opPattern","COPY",EDGE,{"derivedFrom":makeQuery(id+"F4.opRevolve","CAP_EDGE",EDGE,{"disambiguationData":[OSD([sQuery(id+"F3.wireOp",EDGE,"E3")])],"isStart":false}),"instanceName":"34"});
            circularPattern(context, id + "F49", {"entities" : qUnion([Q0, Q1]), "axis" : qUnion([Q2]), "angle" : 20 * degree, "instanceCount" : 18});
        }
        {
            var Q0;
            Q0=makeQuery(id+"F12.opExtrude","SWEPT_BODY",BODY,{"disambiguationData":[OSD([sQuery(id+"F11.wireOp",EDGE,"E6")])]});
            var Q1;
            Q1=makeQuery(id+"F13.opExtrude","SWEPT_BODY",BODY,{"disambiguationData":[OSD([sQuery(id+"F11.wireOp",EDGE,"E6")])]});
            var Q2;
            Q2=sQuery(id+"F3.wireOp",EDGE,"E3");
            circularPattern(context, id + "F50", {"entities" : qUnion([Q0, Q1]), "axis" : qUnion([Q2]), "angle" : 20 * degree, "instanceCount" : 18});
        }
        {
            var Q0;
            Q0=makeQuery(id+"F15.opExtrude","SWEPT_BODY",BODY,{"disambiguationData":[OSD([sQuery(id+"F14.wireOp",EDGE,"E7")])]});
            var Q1;
            Q1=makeQuery(id+"F16.opExtrude","SWEPT_BODY",BODY,{"disambiguationData":[OSD([sQuery(id+"F14.wireOp",EDGE,"E7")])]});
            var Q2;
            Q2=makeQuery(id+"F5.opPattern","COPY",EDGE,{"derivedFrom":makeQuery(id+"F4.opRevolve","CAP_EDGE",EDGE,{"disambiguationData":[OSD([sQuery(id+"F3.wireOp",EDGE,"E3")])],"isStart":true}),"instanceName":"1"});
            circularPattern(context, id + "F51", {"entities" : qUnion([Q0, Q1]), "axis" : qUnion([Q2]), "angle" : 20 * degree, "instanceCount" : 18});
        }
        {
            var Q0;
            Q0=makeQuery(id+"F17.opPattern","COPY",BODY,{"derivedFrom":makeQuery(id+"F12.opExtrude","SWEPT_BODY",BODY,{"disambiguationData":[OSD([sQuery(id+"F11.wireOp",EDGE,"E6")])]}),"instanceName":"1"});
            var Q1;
            Q1=makeQuery(id+"F17.opPattern","COPY",BODY,{"derivedFrom":makeQuery(id+"F13.opExtrude","SWEPT_BODY",BODY,{"disambiguationData":[OSD([sQuery(id+"F11.wireOp",EDGE,"E6")])]}),"instanceName":"1"});
            var Q2;
            Q2=makeQuery(id+"F5.opPattern","COPY",EDGE,{"derivedFrom":makeQuery(id+"F4.opRevolve","CAP_EDGE",EDGE,{"disambiguationData":[OSD([sQuery(id+"F3.wireOp",EDGE,"E3")])],"isStart":true}),"instanceName":"2"});
            circularPattern(context, id + "F52", {"entities" : qUnion([Q0, Q1]), "axis" : qUnion([Q2]), "angle" : 20 * degree, "instanceCount" : 18});
        }
        {
            var Q0;
            Q0=makeQuery(id+"F18.opPattern","COPY",BODY,{"derivedFrom":makeQuery(id+"F15.opExtrude","SWEPT_BODY",BODY,{"disambiguationData":[OSD([sQuery(id+"F14.wireOp",EDGE,"E7")])]}),"instanceName":"17"});
            var Q1;
            Q1=makeQuery(id+"F18.opPattern","COPY",BODY,{"derivedFrom":makeQuery(id+"F16.opExtrude","SWEPT_BODY",BODY,{"disambiguationData":[OSD([sQuery(id+"F14.wireOp",EDGE,"E7")])]}),"instanceName":"17"});
            var Q2;
            Q2=makeQuery(id+"F5.opPattern","COPY",EDGE,{"derivedFrom":makeQuery(id+"F4.opRevolve","CAP_EDGE",EDGE,{"disambiguationData":[OSD([sQuery(id+"F3.wireOp",EDGE,"E3")])],"isStart":true}),"instanceName":"3"});
            circularPattern(context, id + "F53", {"entities" : qUnion([Q0, Q1]), "axis" : qUnion([Q2]), "angle" : 20 * degree, "instanceCount" : 18});
        }
        {
            var Q0;
            Q0=makeQuery(id+"F17.opPattern","COPY",BODY,{"derivedFrom":makeQuery(id+"F12.opExtrude","SWEPT_BODY",BODY,{"disambiguationData":[OSD([sQuery(id+"F11.wireOp",EDGE,"E6")])]}),"instanceName":"2"});
            var Q1;
            Q1=makeQuery(id+"F17.opPattern","COPY",BODY,{"derivedFrom":makeQuery(id+"F13.opExtrude","SWEPT_BODY",BODY,{"disambiguationData":[OSD([sQuery(id+"F11.wireOp",EDGE,"E6")])]}),"instanceName":"2"});
            var Q2;
            Q2=makeQuery(id+"F5.opPattern","COPY",EDGE,{"derivedFrom":makeQuery(id+"F4.opRevolve","CAP_EDGE",EDGE,{"disambiguationData":[OSD([sQuery(id+"F3.wireOp",EDGE,"E3")])],"isStart":true}),"instanceName":"4"});
            circularPattern(context, id + "F54", {"entities" : qUnion([Q0, Q1]), "axis" : qUnion([Q2]), "angle" : 20 * degree, "instanceCount" : 18});
        }
    });
